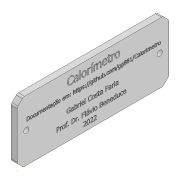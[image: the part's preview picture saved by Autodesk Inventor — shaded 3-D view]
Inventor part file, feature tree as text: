
AUTODESK INVENTOR PART (.ipt)
format: ipt  version: 2020 (Build 240168000, 168)  size: 2,632,192 bytes
history: native  units: mm
features: sketch x4, extrude x3, other x1, chamfer x1, fillet x1
ambient origin geometry x8: Origin, YZ Plane, XZ Plane, XY Plane, X Axis, Y Axis, Z Axis, Center Point
bodies: Body1 (feature_tree)
feature tree (10):
  other  "Sólido1"
  extrude  "Extrusão1"  Depth=100.0mm
  extrude  "Extrusão2"  Depth=3.5mm
  extrude  "Extrusão3"  Depth=6.0mm
  chamfer  "Chanfro1"  Distance=4.0mm
  fillet  "Arredondamento1"  Radius=40.0mm
  sketch  "Esboço4"  dims[d7=6.0mm d8=4.0mm d9=0.0mm d10=40.0mm d11=20.0mm d12=20.0mm d13=1.0mm d14=0.0mm d15=4.0mm d16=2.0mm d17=45.0deg d18=2.0mm]
  sketch  "Esboço1"  dims[d0=100.0mm d1=40.0mm]
  sketch  "Esboço2"  dims[d2=4.0mm d3=0.0mm d4=3.5mm]
  sketch  "Esboço3"  dims[d5=3.5mm d6=6.0mm]
